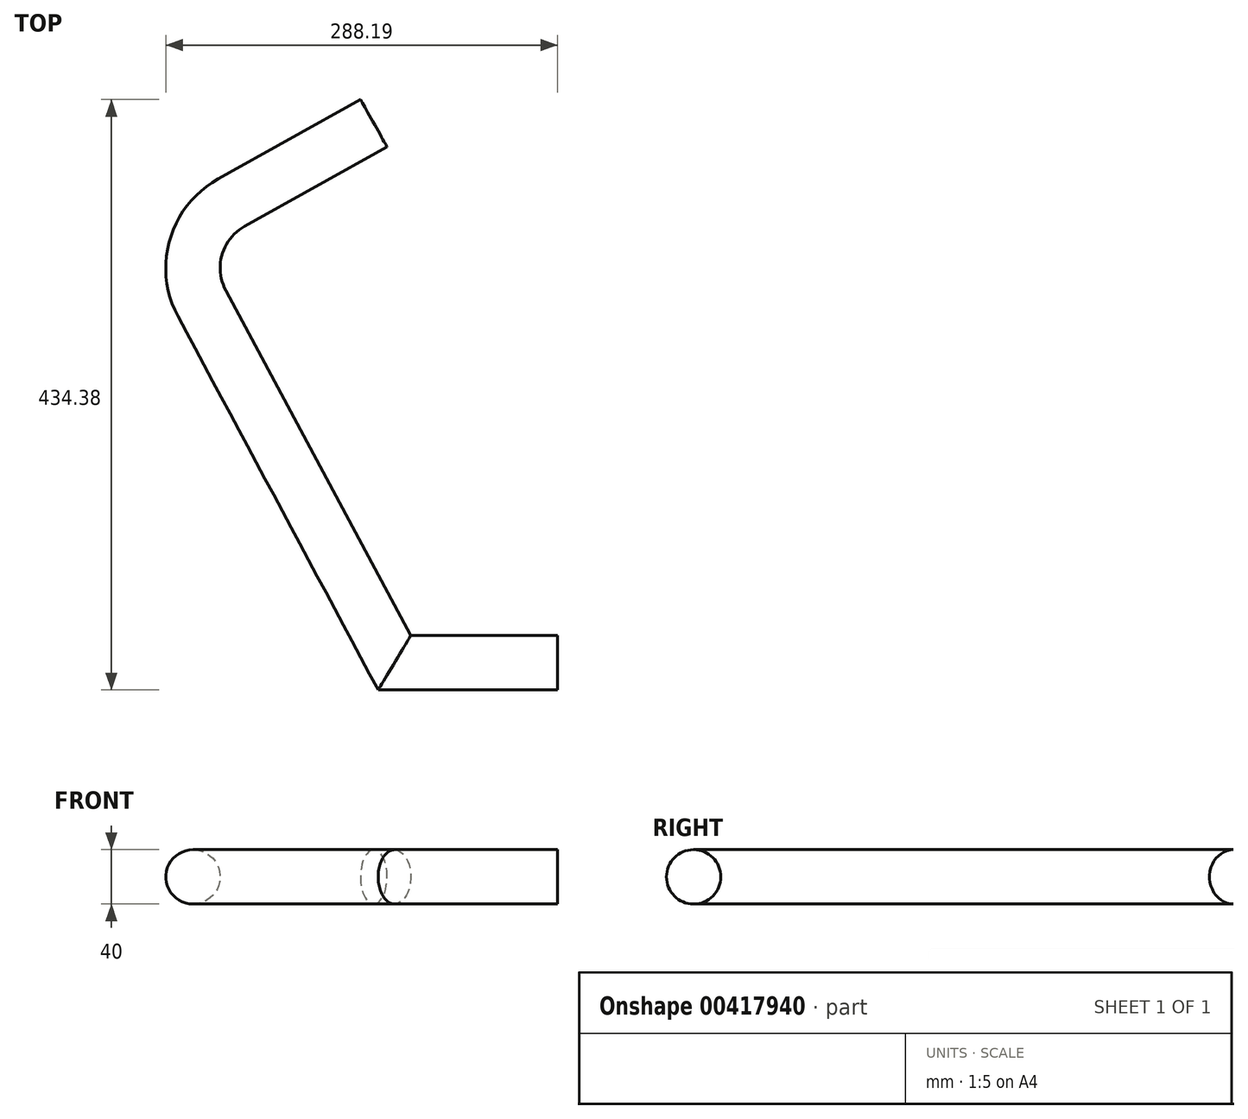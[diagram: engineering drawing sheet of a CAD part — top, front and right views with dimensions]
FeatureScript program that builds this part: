
annotation { "Feature Type Name" : "Feature", "Feature Type Description" : "" }
export const myFeature = defineFeature(function(context is Context, id is Id, definition is map)
    precondition{}
    {
        {
            var Q0;
            Q0=qCreatedBy(makeId("Right.planeOp"),FACE);
            var sketch = newSketch(context, id + "F0", { "sketchPlane" : qUnion([Q0])});
            skCircle(sketch, "E0", {"center": v(0, 0) * mm, "radius": 20 * mm});
            skSolve(sketch);
        }
        {
            var Q0;
            Q0=qCreatedBy(makeId("Top.planeOp"),FACE);
            var sketch = newSketch(context, id + "F1", { "sketchPlane" : qUnion([Q0])});
            skLineSegment(sketch, "E1", {"start": v(0, 0) * mm, "end": v(-120, 0) * mm});
            skLineSegment(sketch, "E2", {"start": v(-120, 0) * mm, "end": v(-261.67, 264.44) * mm});
            skArc(sketch, "E3", {"start": v(-239.98, 338.46) * mm, "mid": v(-265.97, 305.89) * mm, "end": v(-261.67, 264.44) * mm});
            skLineSegment(sketch, "E4", {"start": v(-239.98, 338.46) * mm, "end": v(-135.18, 396.91) * mm});
            skSolve(sketch);
        }
        {
            var Q0;
            Q0=makeQuery(id+"F0.imprint","IMPRINT",FACE,{"disambiguationData":[TD([[makeQuery(id+"F0.imprint","IMPRINT",EDGE,{"derivedFrom":sQuery(id+"F0.wireOp",EDGE,"E0")}),1.0]])]});
            var Q1;
            Q1=sQuery(id+"F1.wireOp",EDGE,"E1");
            var Q2;
            Q2=sQuery(id+"F1.wireOp",EDGE,"E2");
            var Q3;
            Q3=sQuery(id+"F1.wireOp",EDGE,"E3");
            var Q4;
            Q4=sQuery(id+"F1.wireOp",EDGE,"E4");
            sweep(context, id + "F2", {"profiles" : qUnion([Q0]), "path" : qUnion([Q1, Q2, Q3, Q4])});
        }
    });
